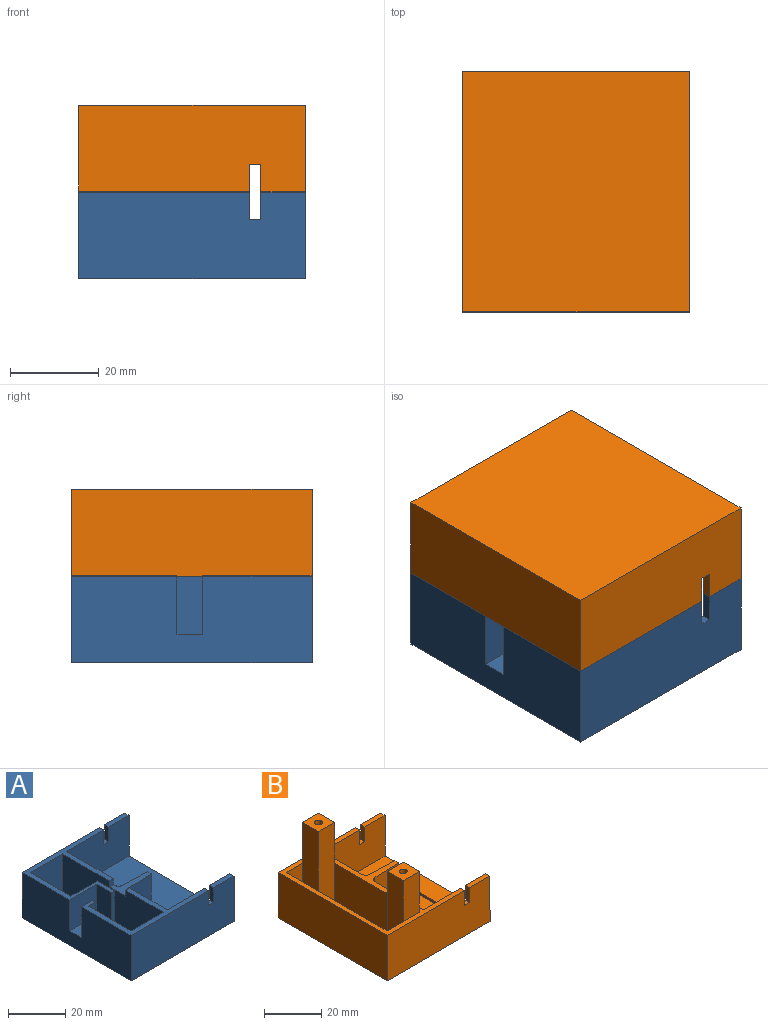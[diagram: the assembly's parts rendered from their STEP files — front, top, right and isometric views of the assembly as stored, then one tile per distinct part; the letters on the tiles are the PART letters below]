
ASSEMBLY  parts=2 mates=1
PART A: 58 faces, bbox 51x54x19.5 mm
  f0: plane 10x2mm, normal (0,0,1), area 20mm2, adj f4,f5,f18,f51
  f1: plane 38.5x30.75mm, normal (0,0,1), area 195.2mm2, adj f4,f5,f12,f16,f20,f21,f24,f25
  f2: plane 10x2mm, normal (0,0,1), area 20mm2, adj f6,f17,f18,f48
  f3: plane 38.5x24.63mm, normal (0,0,1), area 164.8mm2, adj f6,f16,f17,f21,f22,f23,f24,f27
  f4: plane 51x19.5mm, normal (0,1,0), area 978.8mm2, adj f0,f1,f16,f18,f19,f51,f52,f53
  f5: plane 31x17.5mm, normal (0,-1,0), area 526.7mm2, adj f0,f1,f12,f13,f18,f51,f52,f53
  f6: plane 31x17.5mm, normal (0,1,0), area 526.8mm2, adj f2,f3,f13,f18,f27,f48,f49,f50
  f7: cylinder r=2mm len=15mm, axis (0,0,-1), area 40.9mm2, adj f8,f13,f27,f38,f39,f42
  f8: plane 15x12.06mm, normal (0.03,-1,0), area 179.2mm2, adj f7,f9,f14,f35,f37,f39,f42
  f9: plane 15x5.3mm, normal (1,0,0), area 34mm2, adj f8,f10,f13,f30,f34,f38,f39,f42
  f10: plane 15x12.06mm, normal (0.03,1,0), area 179.2mm2, adj f9,f11,f15,f31,f33,f34,f42
  f11: cylinder r=2mm len=15mm, axis (0,0,-1), area 40.9mm2, adj f10,f12,f13,f30,f34,f42
  f12: plane 23.91x17.5mm, normal (1,0,0), area 416.7mm2, adj f1,f5,f11,f13,f40,f42
  f13: plane 50x31mm, normal (0,0,1), area 1472.7mm2, adj f5,f6,f7,f9,f11,f12,f18,f27
  f14: plane 11.14x1.06mm, normal (0,0,1), area 7.8mm2, adj f8,f35,f36,f37
  f15: plane 11.14x1.06mm, normal (0,0,1), area 7.8mm2, adj f10,f31,f32,f33
  f16: plane 54x19.5mm, normal (-1,0,0), area 976.8mm2, adj f1,f3,f4,f17,f19,f43,f44,f47
  f17: plane 51x19.5mm, normal (0,-1,0), area 978.8mm2, adj f2,f3,f16,f18,f19,f48,f49,f50
  f18: plane 54x19.5mm, normal (1,0,0), area 178mm2, adj f0,f2,f4,f5,f6,f13,f17,f19
  f19: plane 54x51mm, normal (0,0,-1), area 2677mm2, adj f4,f16,f17,f18,f56,f57
  f20: plane 17.5x16mm, normal (0,-1,0), area 280mm2, adj f1,f21,f28,f29
  f21: plane 50x17.5mm, normal (-1,0,0), area 855.1mm2, adj f1,f3,f20,f22,f29,f40,f41,f42
  f22: plane 17.5x16mm, normal (0,1,0), area 280mm2, adj f3,f21,f23,f29
  f23: plane 21.25x17.5mm, normal (1,0,0), area 371.9mm2, adj f3,f22,f24,f29
  f24: plane 17.5x13mm, normal (0,-1,0), area 121.5mm2, adj f1,f3,f23,f25,f29,f45,f46,f47
  f25: plane 17.5x8.5mm, normal (1,0,0), area 148.8mm2, adj f1,f24,f26,f29
  f26: plane 17.5x13mm, normal (0,1,0), area 227.5mm2, adj f1,f25,f28,f29
  f27: plane 19.51x17.5mm, normal (1,0,0), area 339.7mm2, adj f3,f6,f7,f13,f41,f42
  f28: plane 20.25x17.5mm, normal (1,0,0), area 354.4mm2, adj f1,f20,f26,f29
  f29: plane 50x16mm, normal (0,0,1), area 664.4mm2, adj f20,f21,f22,f23,f24,f25,f26,f28
  f30: plane 13.96x2mm, normal (0.02,1,0), area 27.9mm2, adj f9,f11,f13,f34
  f31: plane 2x0.7mm, normal (1,-0.03,0), area 1.4mm2, adj f10,f15,f32,f34
  f32: plane 11.11x2mm, normal (-0.03,-1,0), area 22.2mm2, adj f15,f31,f33,f34
  f33: plane 2x0.7mm, normal (-1,0.03,0), area 1.4mm2, adj f10,f15,f32,f34
  f34: plane 13.96x1.97mm, normal (0,0,1), area 14.3mm2, adj f9,f10,f11,f30,f31,f32,f33
  f35: plane 2x0.7mm, normal (-1,-0.03,0), area 1.4mm2, adj f8,f14,f36,f39
  f36: plane 11.11x2mm, normal (-0.03,1,0), area 22.2mm2, adj f14,f35,f37,f39
  f37: plane 2x0.7mm, normal (1,0.03,0), area 1.4mm2, adj f8,f14,f36,f39
  f38: plane 13.96x2mm, normal (0.02,-1,0), area 27.9mm2, adj f7,f9,f13,f39
  f39: plane 13.96x1.97mm, normal (0,0,1), area 14.3mm2, adj f7,f8,f9,f35,f36,f37,f38
  f40: plane 2.5x2mm, normal (0,-1,0), area 5mm2, adj f1,f12,f21,f42
  f41: plane 2.5x2mm, normal (0,1,0), area 5mm2, adj f3,f21,f27,f42
  f42: plane 16x7.98mm, normal (0,0,1), area 49mm2, adj f7,f8,f9,f10,f11,f12,f21,f27
  f43: plane 13.5x13.25mm, normal (0,-1,0), area 178.9mm2, adj f1,f16,f46,f47
  f44: plane 13.25x5.5mm, normal (0,1,0), area 72.9mm2, adj f3,f16,f45,f47
  f45: plane 13.25x1.38mm, normal (1,0,0), area 18.2mm2, adj f3,f24,f44,f47
  f46: plane 13.25x7.13mm, normal (-1,0,0), area 94.4mm2, adj f1,f24,f43,f47
  f47: plane 13.5x7.13mm, normal (0,0,1), area 88.6mm2, adj f16,f24,f43,f44,f45,f46
  f48: plane 6.3x2mm, normal (-1,0,0), area 12.6mm2, adj f2,f6,f17,f50
  f49: plane 6.3x2mm, normal (1,0,0), area 12.6mm2, adj f3,f6,f17,f50
  f50: plane 2.5x2mm, normal (0,0,1), area 5mm2, adj f6,f17,f48,f49
  f51: plane 6.3x2mm, normal (-1,0,0), area 12.6mm2, adj f0,f4,f5,f53
  f52: plane 6.3x2mm, normal (1,0,0), area 12.6mm2, adj f1,f4,f5,f53
  f53: plane 2.5x2mm, normal (0,0,1), area 5mm2, adj f4,f5,f51,f52
  f54: cylinder r=2mm len=4mm, axis (0,0,1), area 6.3mm2, adj f29,f57
  f55: cylinder r=2mm len=4mm, axis (0,0,1), area 6.3mm2, adj f29,f56
  f56: cone r=2mm half-angle=45deg, axis (0,0,-1), area 36.7mm2, adj f19,f55
  f57: cone r=2mm half-angle=45deg, axis (0,0,-1), area 36.7mm2, adj f19,f54
PART B: 59 faces, bbox 51x54x37 mm
  f0: plane 54x38.5mm, normal (0,0,1), area 387.1mm2, adj f3,f4,f7,f8,f10,f11,f14,f15
  f1: plane 10x2mm, normal (0,0,1), area 20mm2, adj f3,f4,f12,f43
  f2: plane 10x2mm, normal (0,0,1), area 20mm2, adj f11,f12,f14,f47
  f3: plane 51x19.5mm, normal (0,1,0), area 978.8mm2, adj f0,f1,f10,f12,f13,f43,f44,f45
  f4: plane 31x17.5mm, normal (0,-1,0), area 526.7mm2, adj f0,f1,f5,f12,f19,f43,f44,f45
  f5: plane 50x31mm, normal (0,0,1), area 1288.7mm2, adj f4,f8,f12,f14,f15,f16,f18,f19
  f6: plane 11.14x1.06mm, normal (0,0,1), area 7.8mm2, adj f17,f36,f37,f38
  f7: plane 17.5x12.06mm, normal (0.03,1,0), area 209.3mm2, adj f0,f8,f9,f18,f30,f32,f33
  f8: cylinder r=2mm len=17.5mm, axis (0,0,-1), area 48.5mm2, adj f0,f5,f7,f19,f29,f30
  f9: plane 11.14x1.06mm, normal (0,0,1), area 7.8mm2, adj f7,f31,f32,f33
  f10: plane 54x19.5mm, normal (-1,0,0), area 1053mm2, adj f0,f3,f11,f13
  f11: plane 51x19.5mm, normal (0,-1,0), area 978.7mm2, adj f0,f2,f10,f12,f13,f46,f47,f48
  f12: plane 54x19.5mm, normal (1,0,0), area 201mm2, adj f1,f2,f3,f4,f5,f11,f13,f14
  f13: plane 54x51mm, normal (0,0,-1), area 2754mm2, adj f3,f10,f11,f12
  f14: plane 31x17.5mm, normal (0,1,0), area 526.7mm2, adj f0,f2,f5,f12,f15,f46,f47,f48
  f15: plane 23.91x17.5mm, normal (1,0,0), area 418.5mm2, adj f0,f5,f14,f16
  f16: cylinder r=2mm len=17.5mm, axis (0,0,-1), area 48.5mm2, adj f0,f5,f15,f17,f34,f35
  f17: plane 17.5x12.06mm, normal (0.03,-1,0), area 209.3mm2, adj f0,f6,f16,f18,f35,f36,f38
  f18: plane 17.5x5.3mm, normal (1,0,0), area 38.5mm2, adj f0,f5,f7,f17,f29,f30,f34,f35
  f19: plane 19.51x17.5mm, normal (1,0,0), area 341.5mm2, adj f0,f4,f5,f8
  f20: plane 17.5x8mm, normal (0,-1,0), area 140mm2, adj f0,f21,f27,f28
  f21: plane 35x8mm, normal (-1,0,0), area 280mm2, adj f20,f22,f28,f49,f51
  f22: plane 35x8mm, normal (0,-1,0), area 280mm2, adj f21,f23,f28,f50,f51
  f23: plane 34x17.5mm, normal (-1,0,0), area 595mm2, adj f0,f22,f24,f28
  f24: plane 35x8mm, normal (0,1,0), area 280mm2, adj f23,f25,f28,f53,f54
  f25: plane 35x8mm, normal (-1,0,0), area 280mm2, adj f24,f26,f28,f52,f54
  f26: plane 17.5x8mm, normal (0,1,0), area 140mm2, adj f0,f25,f27,f28
  f27: plane 50x17.5mm, normal (1,0,0), area 875mm2, adj f0,f20,f26,f28
  f28: plane 50x16mm, normal (0,0,1), area 672mm2, adj f20,f21,f22,f23,f24,f25,f26,f27
  f29: plane 13.96x2mm, normal (0.02,1,0), area 27.9mm2, adj f5,f8,f18,f30
  f30: plane 13.96x1.97mm, normal (0,0,1), area 14.3mm2, adj f7,f8,f18,f29,f31,f32,f33
  f31: plane 11.11x2mm, normal (-0.03,-1,0), area 22.2mm2, adj f9,f30,f32,f33
  f32: plane 2x0.7mm, normal (-1,0.03,0), area 1.4mm2, adj f7,f9,f30,f31
  f33: plane 2x0.7mm, normal (1,-0.03,0), area 1.4mm2, adj f7,f9,f30,f31
  f34: plane 13.96x2mm, normal (0.02,-1,0), area 27.9mm2, adj f5,f16,f18,f35
  f35: plane 13.96x1.97mm, normal (0,0,1), area 14.3mm2, adj f16,f17,f18,f34,f36,f37,f38
  f36: plane 2x0.7mm, normal (-1,-0.03,0), area 1.4mm2, adj f6,f17,f35,f37
  f37: plane 11.11x2mm, normal (-0.03,1,0), area 22.2mm2, adj f6,f35,f36,f38
  f38: plane 2x0.7mm, normal (1,0.03,0), area 1.4mm2, adj f6,f17,f35,f37
  f39: plane 8x1mm, normal (0,1,0), area 8mm2, adj f5,f12,f40,f42
  f40: plane 23x1mm, normal (-1,0,0), area 23mm2, adj f5,f39,f41,f42
  f41: plane 8x1mm, normal (0,-1,0), area 8mm2, adj f5,f12,f40,f42
  f42: plane 23x8mm, normal (0,0,1), area 184mm2, adj f12,f39,f40,f41
  f43: plane 6.3x2mm, normal (-1,0,0), area 12.6mm2, adj f1,f3,f4,f45
  f44: plane 6.3x2mm, normal (1,0,0), area 12.6mm2, adj f0,f3,f4,f45
  f45: plane 2.5x2mm, normal (0,0,1), area 5mm2, adj f3,f4,f43,f44
  f46: plane 6.3x2mm, normal (1,0,0), area 12.6mm2, adj f0,f11,f14,f48
  f47: plane 6.3x2mm, normal (-1,0,0), area 12.6mm2, adj f2,f11,f14,f48
  f48: plane 2.5x2mm, normal (0,0,1), area 5mm2, adj f11,f14,f46,f47
  f49: plane 17.5x8mm, normal (0,1,0), area 140mm2, adj f0,f21,f50,f51
  f50: plane 17.5x8mm, normal (1,0,0), area 140mm2, adj f0,f22,f49,f51
  f51: plane 8x8mm, normal (0,0,1), area 58.1mm2, adj f21,f22,f49,f50,f57
  f52: plane 17.5x8mm, normal (0,-1,0), area 140mm2, adj f0,f25,f53,f54
  f53: plane 17.5x8mm, normal (1,0,0), area 140mm2, adj f0,f24,f52,f54
  f54: plane 8x8mm, normal (0,0,1), area 58.1mm2, adj f24,f25,f52,f53,f55
  f55: cylinder r=1.38mm len=10mm, axis (0,0,1), area 86.4mm2, adj f54,f56
  f56: plane 2.75x2.75mm, normal (0,0,1), area 5.9mm2, adj f55
  f57: cylinder r=1.38mm len=10mm, axis (0,0,1), area 86.4mm2, adj f51,f58
  f58: plane 2.75x2.75mm, normal (0,0,1), area 5.9mm2, adj f57
PLACE A t=(-17.62,-13.41,61.38)mm
PLACE B rot(axis=(1,0,0),180deg) t=(-17.62,-13.41,100.36)mm
MATE slider A.f55 <-> B.f55  axis (0,0,1) through (-54.62,44.59,63.38)mm
